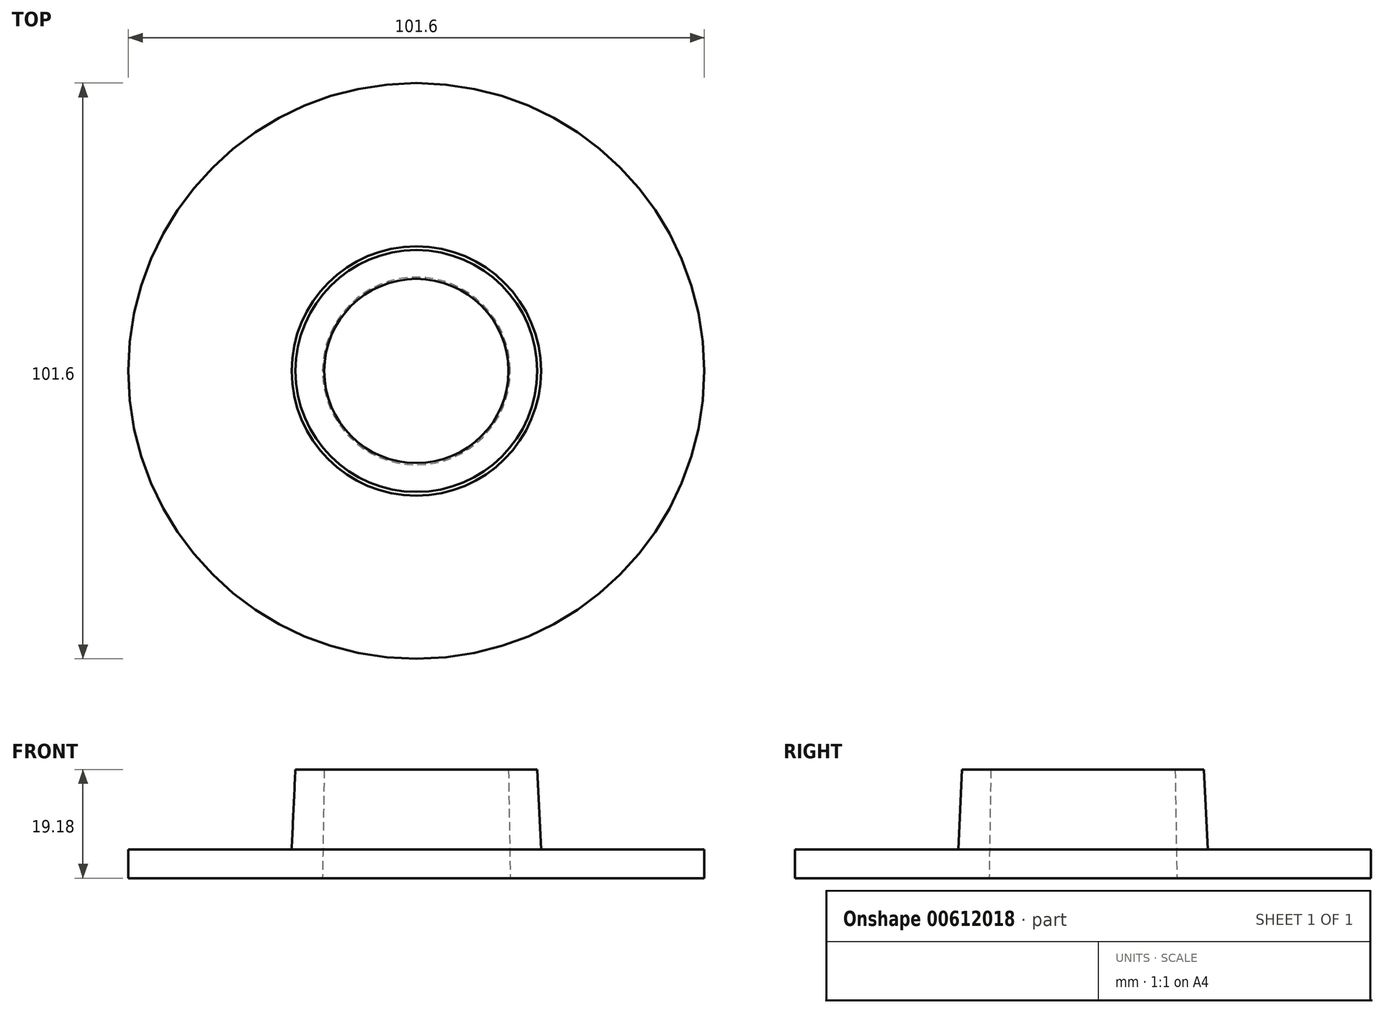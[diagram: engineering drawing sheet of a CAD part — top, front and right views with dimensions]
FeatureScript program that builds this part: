
annotation { "Feature Type Name" : "Feature", "Feature Type Description" : "" }
export const myFeature = defineFeature(function(context is Context, id is Id, definition is map)
    precondition{}
    {
        {
            var Q0;
            Q0=qCreatedBy(makeId("Front.planeOp"),FACE);
            var sketch = newSketch(context, id + "F0", { "sketchPlane" : qUnion([Q0])});
            skLineSegment(sketch, "E0", {"start": v(0, 0) * mm, "end": v(0, 19.1) * mm, "construction": true});
            skLineSegment(sketch, "E1", {"start": v(0, 19.1) * mm, "end": v(-16.26, 19.1) * mm, "construction": true});
            skLineSegment(sketch, "E2", {"start": v(0, 0) * mm, "end": v(-16.56, 0) * mm, "construction": true});
            skLineSegment(sketch, "E3", {"start": v(-16.56, 0) * mm, "end": v(-16.26, 19.1) * mm});
            skLineSegment(sketch, "E4", {"start": v(-16.56, 0) * mm, "end": v(-50.8, 0) * mm});
            skLineSegment(sketch, "E5", {"start": v(-50.8, 0) * mm, "end": v(-50.8, 5.08) * mm});
            skLineSegment(sketch, "E6", {"start": v(-50.8, 5.08) * mm, "end": v(-22, 5.08) * mm});
            skLineSegment(sketch, "E7", {"start": v(-16.26, 19.1) * mm, "end": v(-21.34, 19.18) * mm});
            skLineSegment(sketch, "E8", {"start": v(-21.34, 19.18) * mm, "end": v(-22, 5.08) * mm});
            skSolve(sketch);
        }
        {
            var Q0;
            Q0 = qSketchRegion(id + "F0", true);
            var Q1;
            Q1=sQuery(id+"F0.wireOp",EDGE,"E0");
            revolve(context, id + "F1", {"entities" : qUnion([Q0]), "axis" : qUnion([Q1]), "revolveType" : RevolveType.FULL});
        }
    });
